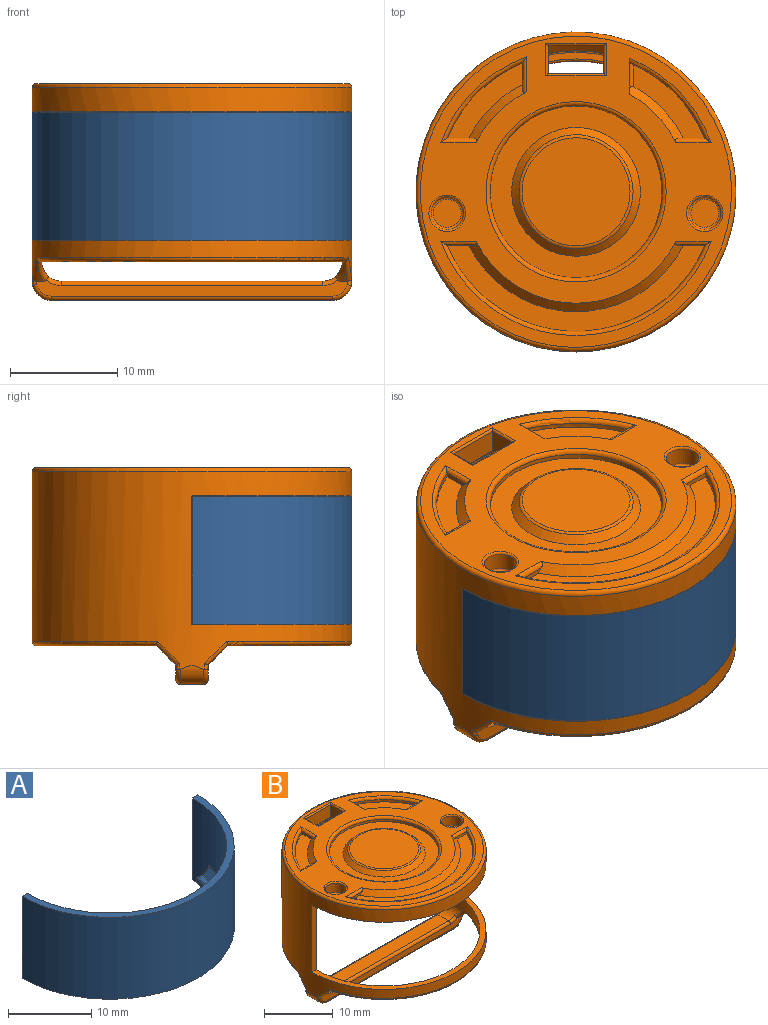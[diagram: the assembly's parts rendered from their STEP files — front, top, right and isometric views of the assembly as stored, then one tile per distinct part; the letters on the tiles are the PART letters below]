
ASSEMBLY  parts=2 mates=1
PART A: 37 faces, bbox 100.4x15.2x41.7 mm
  f0: cylinder r=14mm len=28mm, axis (0,0,-1), area 449mm2, adj f8,f9,f10,f11,f25,f26,f29,f30
  f1: plane 25.27x10.03mm, normal (0,0,1), area 20.8mm2, adj f12,f13,f14,f15
  f2: cylinder r=12.2mm len=23.68mm, axis (0,0,-1), area 16.2mm2, adj f13,f21,f22,f23
  f3: plane 26.8x10.82mm, normal (0,0,-1), area 48.7mm2, adj f22,f31,f32,f36
  f4: plane 1.36x1.12mm, normal (-0.22,0.97,0), area 0.9mm2, adj f14,f19,f23,f24,f32,f33
  f5: cone r=13.1mm half-angle=45deg, axis (0,0,1), area 39.9mm2, adj f15,f20,f24,f25
  f6: plane 1.36x1.12mm, normal (0.22,0.97,0), area 0.9mm2, adj f12,f16,f20,f21,f30,f31
  f7: cylinder r=14.9mm len=29.8mm, axis (0,0,-1), area 561.7mm2, adj f8,f9,f10,f11
  f8: plane 12x0.9mm, normal (0,1,0), area 10.8mm2, adj f0,f7,f10,f11
  f9: plane 12x0.9mm, normal (0,1,0), area 10.8mm2, adj f0,f7,f10,f11
  f10: plane 29.8x14.9mm, normal (0,0,-1), area 40.9mm2, adj f0,f7,f8,f9
  f11: plane 29.8x14.9mm, normal (0,0,1), area 40.9mm2, adj f0,f7,f8,f9
  f12: cylinder r=0.2mm len=0.65mm, axis (0.97,-0.22,0), area 0.2mm2, adj f1,f6,f16,f17
  f13: torus R=12.4mm, axis (0,0,-1), area 10.2mm2, adj f1,f2,f17,f18
  f14: cylinder r=0.2mm len=0.65mm, axis (0.97,0.22,0), area 0.2mm2, adj f1,f4,f18,f19
  f15: torus R=13.02mm, axis (0,0,-1), area 5.5mm2, adj f1,f5,f16,f19
  f16: bspline ~0.39x0.28mm, area 0.1mm2, adj f6,f12,f15,f20
  f17: sphere r=0.2mm, area 0.1mm2, adj f12,f13,f21
  f18: sphere r=0.2mm, area 0mm2, adj f13,f14,f23
  f19: bspline ~0.4x0.29mm, area 0.1mm2, adj f4,f14,f15,f24
  f20: bspline ~41.73x40.71mm, area 0.3mm2, adj f5,f6,f16,f26
  f21: cylinder r=0.2mm len=0.5mm, axis (0,0,-1), area 0.2mm2, adj f2,f6,f17,f27
  f22: torus R=12.4mm, axis (0,0,1), area 10.2mm2, adj f2,f3,f27,f28
  f23: cylinder r=0.2mm len=0.5mm, axis (0,0,-1), area 0.2mm2, adj f2,f4,f18,f28
  f24: bspline ~41.73x40.71mm, area 0.3mm2, adj f4,f5,f19,f29
  f25: torus R=13.8mm, axis (0,0,-1), area 5.8mm2, adj f0,f5,f26,f29
  f26: bspline ~0.74x0.44mm, area 0.1mm2, adj f0,f20,f25,f30
  f27: sphere r=0.2mm, area 0.1mm2, adj f21,f22,f31
  f28: sphere r=0.2mm, area 0mm2, adj f22,f23,f32
  f29: bspline ~0.64x0.46mm, area 0.1mm2, adj f0,f24,f25,f33
  f30: cylinder r=0.2mm len=1.12mm, axis (0,0,-1), area 0.4mm2, adj f0,f6,f26,f34
  f31: cylinder r=0.2mm len=1.41mm, axis (-0.97,0.22,0), area 0.4mm2, adj f3,f6,f27,f34
  f32: cylinder r=0.2mm len=1.41mm, axis (-0.97,-0.22,0), area 0.4mm2, adj f3,f4,f28,f35
  f33: cylinder r=0.2mm len=1.12mm, axis (0,0,-1), area 0.4mm2, adj f0,f4,f29,f35
  f34: bspline ~0.48x0.47mm, area 0.1mm2, adj f0,f30,f31,f36
  f35: bspline ~0.49x0.46mm, area 0.1mm2, adj f0,f32,f33,f36
  f36: torus R=13.8mm, axis (0,0,1), area 11.6mm2, adj f0,f3,f34,f35
PART B: 308 faces, bbox 100.4x32.3x47 mm
  f0: plane 29x29mm, normal (0,0,1), area 265.2mm2, adj f227,f264,f266,f274,f275,f276,f277,f285
  f1: plane 4.72x0.2mm, normal (0,0,-1), area 0.6mm2, adj f2,f268
  f2: cylinder r=14mm len=28mm, axis (0,0,-1), area 616.2mm2, adj f1,f179,f180,f182,f183,f184,f186,f198
  f3: plane 1.4x0.2mm, normal (-1,0,0), area 0.3mm2, adj f4,f6,f7,f173
  f4: plane 0.4x0.2mm, normal (0,1,0), area 0.1mm2, adj f3,f5,f7,f173
  f5: plane 1.4x0.2mm, normal (1,0,0), area 0.3mm2, adj f4,f6,f7,f173
  f6: plane 0.4x0.2mm, normal (0,-1,0), area 0.1mm2, adj f3,f5,f7,f173
  f7: plane 1.4x0.4mm, normal (0,0,-1), area 0.6mm2, adj f3,f4,f5,f6
  f8: plane 1.4x0.2mm, normal (-1,0,0), area 0.3mm2, adj f9,f11,f12,f173
  f9: plane 0.4x0.2mm, normal (0,1,0), area 0.1mm2, adj f8,f10,f12,f173
  f10: plane 1.4x0.2mm, normal (1,0,0), area 0.3mm2, adj f9,f11,f12,f173
  f11: plane 0.4x0.2mm, normal (0,-1,0), area 0.1mm2, adj f8,f10,f12,f173
  f12: plane 1.4x0.4mm, normal (0,0,-1), area 0.6mm2, adj f8,f9,f10,f11
  f13: plane 1.4x0.2mm, normal (-1,0,0), area 0.3mm2, adj f14,f16,f17,f173
  f14: plane 0.4x0.2mm, normal (0,1,0), area 0.1mm2, adj f13,f15,f17,f173
  f15: plane 1.4x0.2mm, normal (1,0,0), area 0.3mm2, adj f14,f16,f17,f173
  f16: plane 0.4x0.2mm, normal (0,-1,0), area 0.1mm2, adj f13,f15,f17,f173
  f17: plane 1.4x0.4mm, normal (0,0,-1), area 0.6mm2, adj f13,f14,f15,f16
  f18: plane 1.4x0.2mm, normal (-1,0,0), area 0.3mm2, adj f19,f21,f22,f173
  f19: plane 0.4x0.2mm, normal (0,1,0), area 0.1mm2, adj f18,f20,f22,f173
  f20: plane 1.4x0.2mm, normal (1,0,0), area 0.3mm2, adj f19,f21,f22,f173
  f21: plane 0.4x0.2mm, normal (0,-1,0), area 0.1mm2, adj f18,f20,f22,f173
  f22: plane 1.4x0.4mm, normal (0,0,-1), area 0.6mm2, adj f18,f19,f20,f21
  f23: plane 1.4x0.2mm, normal (-1,0,0), area 0.3mm2, adj f24,f26,f27,f173
  f24: plane 0.4x0.2mm, normal (0,1,0), area 0.1mm2, adj f23,f25,f27,f173
  f25: plane 1.4x0.2mm, normal (1,0,0), area 0.3mm2, adj f24,f26,f27,f173
  f26: plane 0.4x0.2mm, normal (0,-1,0), area 0.1mm2, adj f23,f25,f27,f173
  f27: plane 1.4x0.4mm, normal (0,0,-1), area 0.6mm2, adj f23,f24,f25,f26
  f28: plane 1.4x0.2mm, normal (-1,0,0), area 0.3mm2, adj f29,f31,f32,f173
  f29: plane 0.4x0.2mm, normal (0,1,0), area 0.1mm2, adj f28,f30,f32,f173
  f30: plane 1.4x0.2mm, normal (1,0,0), area 0.3mm2, adj f29,f31,f32,f173
  f31: plane 0.4x0.2mm, normal (0,-1,0), area 0.1mm2, adj f28,f30,f32,f173
  f32: plane 1.4x0.4mm, normal (0,0,-1), area 0.6mm2, adj f28,f29,f30,f31
  f33: plane 1.4x0.2mm, normal (-1,0,0), area 0.3mm2, adj f34,f36,f37,f173
  f34: plane 0.4x0.2mm, normal (0,1,0), area 0.1mm2, adj f33,f35,f37,f173
  f35: plane 1.4x0.2mm, normal (1,0,0), area 0.3mm2, adj f34,f36,f37,f173
  f36: plane 0.4x0.2mm, normal (0,-1,0), area 0.1mm2, adj f33,f35,f37,f173
  f37: plane 1.4x0.4mm, normal (0,0,-1), area 0.6mm2, adj f33,f34,f35,f36
  f38: plane 1.4x0.2mm, normal (-1,0,0), area 0.3mm2, adj f39,f41,f42,f173
  f39: plane 0.4x0.2mm, normal (0,1,0), area 0.1mm2, adj f38,f40,f42,f173
  f40: plane 1.4x0.2mm, normal (1,0,0), area 0.3mm2, adj f39,f41,f42,f173
  f41: plane 0.4x0.2mm, normal (0,-1,0), area 0.1mm2, adj f38,f40,f42,f173
  f42: plane 1.4x0.4mm, normal (0,0,-1), area 0.6mm2, adj f38,f39,f40,f41
  f43: plane 1.4x0.2mm, normal (-1,0,0), area 0.3mm2, adj f44,f46,f47,f173
  f44: plane 0.4x0.2mm, normal (0,1,0), area 0.1mm2, adj f43,f45,f47,f173
  f45: plane 1.4x0.2mm, normal (1,0,0), area 0.3mm2, adj f44,f46,f47,f173
  f46: plane 0.4x0.2mm, normal (0,-1,0), area 0.1mm2, adj f43,f45,f47,f173
  f47: plane 1.4x0.4mm, normal (0,0,-1), area 0.6mm2, adj f43,f44,f45,f46
  f48: plane 1.4x0.2mm, normal (-1,0,0), area 0.3mm2, adj f49,f51,f52,f173
  f49: plane 0.4x0.2mm, normal (0,1,0), area 0.1mm2, adj f48,f50,f52,f173
  f50: plane 1.4x0.2mm, normal (1,0,0), area 0.3mm2, adj f49,f51,f52,f173
  f51: plane 0.4x0.2mm, normal (0,-1,0), area 0.1mm2, adj f48,f50,f52,f173
  f52: plane 1.4x0.4mm, normal (0,0,-1), area 0.6mm2, adj f48,f49,f50,f51
  f53: plane 1.4x0.2mm, normal (-1,0,0), area 0.3mm2, adj f54,f56,f57,f173
  f54: plane 0.4x0.2mm, normal (0,1,0), area 0.1mm2, adj f53,f55,f57,f173
  f55: plane 1.4x0.2mm, normal (1,0,0), area 0.3mm2, adj f54,f56,f57,f173
  f56: plane 0.4x0.2mm, normal (0,-1,0), area 0.1mm2, adj f53,f55,f57,f173
  f57: plane 1.4x0.4mm, normal (0,0,-1), area 0.6mm2, adj f53,f54,f55,f56
  f58: plane 1.4x0.2mm, normal (-1,0,0), area 0.3mm2, adj f59,f61,f62,f173
  f59: plane 0.4x0.2mm, normal (0,1,0), area 0.1mm2, adj f58,f60,f62,f173
  f60: plane 1.4x0.2mm, normal (1,0,0), area 0.3mm2, adj f59,f61,f62,f173
  f61: plane 0.4x0.2mm, normal (0,-1,0), area 0.1mm2, adj f58,f60,f62,f173
  f62: plane 1.4x0.4mm, normal (0,0,-1), area 0.6mm2, adj f58,f59,f60,f61
  f63: plane 1.4x0.2mm, normal (-1,0,0), area 0.3mm2, adj f64,f66,f67,f173
  f64: plane 0.4x0.2mm, normal (0,1,0), area 0.1mm2, adj f63,f65,f67,f173
  f65: plane 1.4x0.2mm, normal (1,0,0), area 0.3mm2, adj f64,f66,f67,f173
  f66: plane 0.4x0.2mm, normal (0,-1,0), area 0.1mm2, adj f63,f65,f67,f173
  f67: plane 1.4x0.4mm, normal (0,0,-1), area 0.6mm2, adj f63,f64,f65,f66
  f68: plane 1.4x0.2mm, normal (-1,0,0), area 0.3mm2, adj f69,f71,f72,f173
  f69: plane 0.4x0.2mm, normal (0,1,0), area 0.1mm2, adj f68,f70,f72,f173
  f70: plane 1.4x0.2mm, normal (1,0,0), area 0.3mm2, adj f69,f71,f72,f173
  f71: plane 0.4x0.2mm, normal (0,-1,0), area 0.1mm2, adj f68,f70,f72,f173
  f72: plane 1.4x0.4mm, normal (0,0,-1), area 0.6mm2, adj f68,f69,f70,f71
  f73: plane 1.4x0.2mm, normal (-1,0,0), area 0.3mm2, adj f74,f76,f77,f173
  f74: plane 0.4x0.2mm, normal (0,1,0), area 0.1mm2, adj f73,f75,f77,f173
  f75: plane 1.4x0.2mm, normal (1,0,0), area 0.3mm2, adj f74,f76,f77,f173
  f76: plane 0.4x0.2mm, normal (0,-1,0), area 0.1mm2, adj f73,f75,f77,f173
  f77: plane 1.4x0.4mm, normal (0,0,-1), area 0.6mm2, adj f73,f74,f75,f76
  f78: plane 1.4x0.2mm, normal (-1,0,0), area 0.3mm2, adj f79,f81,f82,f173
  f79: plane 0.4x0.2mm, normal (0,1,0), area 0.1mm2, adj f78,f80,f82,f173
  f80: plane 1.4x0.2mm, normal (1,0,0), area 0.3mm2, adj f79,f81,f82,f173
  f81: plane 0.4x0.2mm, normal (0,-1,0), area 0.1mm2, adj f78,f80,f82,f173
  f82: plane 1.4x0.4mm, normal (0,0,-1), area 0.6mm2, adj f78,f79,f80,f81
  f83: plane 1.4x0.2mm, normal (-1,0,0), area 0.3mm2, adj f84,f86,f87,f173
  f84: plane 0.4x0.2mm, normal (0,1,0), area 0.1mm2, adj f83,f85,f87,f173
  f85: plane 1.4x0.2mm, normal (1,0,0), area 0.3mm2, adj f84,f86,f87,f173
  f86: plane 0.4x0.2mm, normal (0,-1,0), area 0.1mm2, adj f83,f85,f87,f173
  f87: plane 1.4x0.4mm, normal (0,0,-1), area 0.6mm2, adj f83,f84,f85,f86
  f88: plane 1.4x0.2mm, normal (-1,0,0), area 0.3mm2, adj f89,f91,f92,f173
  f89: plane 0.4x0.2mm, normal (0,1,0), area 0.1mm2, adj f88,f90,f92,f173
  f90: plane 1.4x0.2mm, normal (1,0,0), area 0.3mm2, adj f89,f91,f92,f173
  f91: plane 0.4x0.2mm, normal (0,-1,0), area 0.1mm2, adj f88,f90,f92,f173
  f92: plane 1.4x0.4mm, normal (0,0,-1), area 0.6mm2, adj f88,f89,f90,f91
  f93: plane 1.4x0.2mm, normal (-1,0,0), area 0.3mm2, adj f94,f96,f97,f173
  f94: plane 0.4x0.2mm, normal (0,1,0), area 0.1mm2, adj f93,f95,f97,f173
  f95: plane 1.4x0.2mm, normal (1,0,0), area 0.3mm2, adj f94,f96,f97,f173
  f96: plane 0.4x0.2mm, normal (0,-1,0), area 0.1mm2, adj f93,f95,f97,f173
  f97: plane 1.4x0.4mm, normal (0,0,-1), area 0.6mm2, adj f93,f94,f95,f96
  f98: plane 1.4x0.2mm, normal (-1,0,0), area 0.3mm2, adj f99,f101,f102,f173
  f99: plane 0.4x0.2mm, normal (0,1,0), area 0.1mm2, adj f98,f100,f102,f173
  f100: plane 1.4x0.2mm, normal (1,0,0), area 0.3mm2, adj f99,f101,f102,f173
  f101: plane 0.4x0.2mm, normal (0,-1,0), area 0.1mm2, adj f98,f100,f102,f173
  f102: plane 1.4x0.4mm, normal (0,0,-1), area 0.6mm2, adj f98,f99,f100,f101
  f103: plane 1.4x0.2mm, normal (-1,0,0), area 0.3mm2, adj f104,f106,f107,f173
  f104: plane 0.4x0.2mm, normal (0,1,0), area 0.1mm2, adj f103,f105,f107,f173
  f105: plane 1.4x0.2mm, normal (1,0,0), area 0.3mm2, adj f104,f106,f107,f173
  f106: plane 0.4x0.2mm, normal (0,-1,0), area 0.1mm2, adj f103,f105,f107,f173
  f107: plane 1.4x0.4mm, normal (0,0,-1), area 0.6mm2, adj f103,f104,f105,f106
  f108: plane 1.4x0.2mm, normal (-1,0,0), area 0.3mm2, adj f109,f111,f112,f173
  f109: plane 0.4x0.2mm, normal (0,1,0), area 0.1mm2, adj f108,f110,f112,f173
  f110: plane 1.4x0.2mm, normal (1,0,0), area 0.3mm2, adj f109,f111,f112,f173
  f111: plane 0.4x0.2mm, normal (0,-1,0), area 0.1mm2, adj f108,f110,f112,f173
  f112: plane 1.4x0.4mm, normal (0,0,-1), area 0.6mm2, adj f108,f109,f110,f111
  f113: plane 1.4x0.2mm, normal (-1,0,0), area 0.3mm2, adj f114,f116,f117,f173
  f114: plane 0.4x0.2mm, normal (0,1,0), area 0.1mm2, adj f113,f115,f117,f173
  f115: plane 1.4x0.2mm, normal (1,0,0), area 0.3mm2, adj f114,f116,f117,f173
  f116: plane 0.4x0.2mm, normal (0,-1,0), area 0.1mm2, adj f113,f115,f117,f173
  f117: plane 1.4x0.4mm, normal (0,0,-1), area 0.6mm2, adj f113,f114,f115,f116
  f118: plane 1.4x0.2mm, normal (-1,0,0), area 0.3mm2, adj f119,f121,f122,f173
  f119: plane 0.4x0.2mm, normal (0,1,0), area 0.1mm2, adj f118,f120,f122,f173
  f120: plane 1.4x0.2mm, normal (1,0,0), area 0.3mm2, adj f119,f121,f122,f173
  f121: plane 0.4x0.2mm, normal (0,-1,0), area 0.1mm2, adj f118,f120,f122,f173
  f122: plane 1.4x0.4mm, normal (0,0,-1), area 0.6mm2, adj f118,f119,f120,f121
  f123: plane 1.4x0.2mm, normal (-1,0,0), area 0.3mm2, adj f124,f126,f127,f173
  f124: plane 0.4x0.2mm, normal (0,1,0), area 0.1mm2, adj f123,f125,f127,f173
  f125: plane 1.4x0.2mm, normal (1,0,0), area 0.3mm2, adj f124,f126,f127,f173
  f126: plane 0.4x0.2mm, normal (0,-1,0), area 0.1mm2, adj f123,f125,f127,f173
  f127: plane 1.4x0.4mm, normal (0,0,-1), area 0.6mm2, adj f123,f124,f125,f126
  f128: plane 1.4x0.2mm, normal (-1,0,0), area 0.3mm2, adj f129,f131,f132,f173
  f129: plane 0.4x0.2mm, normal (0,1,0), area 0.1mm2, adj f128,f130,f132,f173
  f130: plane 1.4x0.2mm, normal (1,0,0), area 0.3mm2, adj f129,f131,f132,f173
  f131: plane 0.4x0.2mm, normal (0,-1,0), area 0.1mm2, adj f128,f130,f132,f173
  f132: plane 1.4x0.4mm, normal (0,0,-1), area 0.6mm2, adj f128,f129,f130,f131
  f133: plane 1.4x0.2mm, normal (-1,0,0), area 0.3mm2, adj f134,f136,f137,f173
  f134: plane 0.4x0.2mm, normal (0,1,0), area 0.1mm2, adj f133,f135,f137,f173
  f135: plane 1.4x0.2mm, normal (1,0,0), area 0.3mm2, adj f134,f136,f137,f173
  f136: plane 0.4x0.2mm, normal (0,-1,0), area 0.1mm2, adj f133,f135,f137,f173
  f137: plane 1.4x0.4mm, normal (0,0,-1), area 0.6mm2, adj f133,f134,f135,f136
  f138: plane 1.4x0.2mm, normal (-1,0,0), area 0.3mm2, adj f139,f141,f142,f173
  f139: plane 0.4x0.2mm, normal (0,1,0), area 0.1mm2, adj f138,f140,f142,f173
  f140: plane 1.4x0.2mm, normal (1,0,0), area 0.3mm2, adj f139,f141,f142,f173
  f141: plane 0.4x0.2mm, normal (0,-1,0), area 0.1mm2, adj f138,f140,f142,f173
  f142: plane 1.4x0.4mm, normal (0,0,-1), area 0.6mm2, adj f138,f139,f140,f141
  f143: plane 1.4x0.2mm, normal (-1,0,0), area 0.3mm2, adj f144,f146,f147,f173
  f144: plane 0.4x0.2mm, normal (0,1,0), area 0.1mm2, adj f143,f145,f147,f173
  f145: plane 1.4x0.2mm, normal (1,0,0), area 0.3mm2, adj f144,f146,f147,f173
  f146: plane 0.4x0.2mm, normal (0,-1,0), area 0.1mm2, adj f143,f145,f147,f173
  f147: plane 1.4x0.4mm, normal (0,0,-1), area 0.6mm2, adj f143,f144,f145,f146
  f148: plane 1.4x0.2mm, normal (-1,0,0), area 0.3mm2, adj f149,f151,f152,f173
  f149: plane 0.4x0.2mm, normal (0,1,0), area 0.1mm2, adj f148,f150,f152,f173
  f150: plane 1.4x0.2mm, normal (1,0,0), area 0.3mm2, adj f149,f151,f152,f173
  f151: plane 0.4x0.2mm, normal (0,-1,0), area 0.1mm2, adj f148,f150,f152,f173
  f152: plane 1.4x0.4mm, normal (0,0,-1), area 0.6mm2, adj f148,f149,f150,f151
  f153: plane 1.4x0.2mm, normal (-1,0,0), area 0.3mm2, adj f154,f156,f157,f173
  f154: plane 0.4x0.2mm, normal (0,1,0), area 0.1mm2, adj f153,f155,f157,f173
  f155: plane 1.4x0.2mm, normal (1,0,0), area 0.3mm2, adj f154,f156,f157,f173
  f156: plane 0.4x0.2mm, normal (0,-1,0), area 0.1mm2, adj f153,f155,f157,f173
  f157: plane 1.4x0.4mm, normal (0,0,-1), area 0.6mm2, adj f153,f154,f155,f156
  f158: plane 1.4x0.2mm, normal (-1,0,0), area 0.3mm2, adj f159,f161,f162,f173
  f159: plane 0.4x0.2mm, normal (0,1,0), area 0.1mm2, adj f158,f160,f162,f173
  f160: plane 1.4x0.2mm, normal (1,0,0), area 0.3mm2, adj f159,f161,f162,f173
  f161: plane 0.4x0.2mm, normal (0,-1,0), area 0.1mm2, adj f158,f160,f162,f173
  f162: plane 1.4x0.4mm, normal (0,0,-1), area 0.6mm2, adj f158,f159,f160,f161
  f163: plane 1.4x0.2mm, normal (-1,0,0), area 0.3mm2, adj f164,f166,f167,f173
  f164: plane 0.4x0.2mm, normal (0,1,0), area 0.1mm2, adj f163,f165,f167,f173
  f165: plane 1.4x0.2mm, normal (1,0,0), area 0.3mm2, adj f164,f166,f167,f173
  f166: plane 0.4x0.2mm, normal (0,-1,0), area 0.1mm2, adj f163,f165,f167,f173
  f167: plane 1.4x0.4mm, normal (0,0,-1), area 0.6mm2, adj f163,f164,f165,f166
  f168: plane 1.4x0.2mm, normal (-1,0,0), area 0.3mm2, adj f169,f171,f172,f173
  f169: plane 0.4x0.2mm, normal (0,1,0), area 0.1mm2, adj f168,f170,f172,f173
  f170: plane 1.4x0.2mm, normal (1,0,0), area 0.3mm2, adj f169,f171,f172,f173
  f171: plane 0.4x0.2mm, normal (0,-1,0), area 0.1mm2, adj f168,f170,f172,f173
  f172: plane 1.4x0.4mm, normal (0,0,-1), area 0.6mm2, adj f168,f169,f170,f171
  f173: plane 26.2x2.2mm, normal (0,0,-1), area 38mm2, adj f3,f4,f5,f6,f8,f9,f10,f11
  f174: cylinder r=1.8mm len=2.2mm, axis (0,1,0), area 5.8mm2, adj f173,f181,f218,f222
  f175: cylinder r=1.8mm len=2.2mm, axis (0,1,0), area 5.8mm2, adj f173,f181,f215,f226
  f176: plane 28.92x1.49mm, normal (0,-1,0), area 29.3mm2, adj f207,f210,f219,f220,f222,f223,f224,f225
  f177: plane 28.92x1.49mm, normal (0,1,0), area 29.3mm2, adj f208,f209,f211,f213,f214,f215,f216,f217
  f178: plane 28.32x12.16mm, normal (0,0,-1), area 11.8mm2, adj f184,f186,f212,f228,f234,f238
  f179: plane 28.32x14.53mm, normal (0,0,-1), area 20mm2, adj f2,f184,f186,f221,f229,f233
  f180: plane 29.8x14.9mm, normal (0,0,1), area 40.9mm2, adj f2,f181,f182,f183
  f181: cylinder r=14.9mm len=29.8mm, axis (0,0,-1), area 936.9mm2, adj f174,f175,f180,f182,f183,f198,f211,f212
  f182: plane 12x0.9mm, normal (0,-1,0), area 10.8mm2, adj f2,f180,f181,f198
  f183: plane 12x0.9mm, normal (0,-1,0), area 10.8mm2, adj f2,f180,f181,f198
  f184: cylinder r=1.8mm len=5.47mm, axis (0,1,0), area 8.9mm2, adj f2,f178,f179,f185,f228,f232,f233,f237
  f185: plane 24.4x2.2mm, normal (0,0,1), area 53.7mm2, adj f184,f186,f231,f236
  f186: cylinder r=1.8mm len=5.47mm, axis (0,1,0), area 8.9mm2, adj f2,f178,f179,f185,f228,f229,f230,f234
  f187: plane 1.4x0.2mm, normal (-1,0,0), area 0.3mm2, adj f173,f188,f190,f191
  f188: plane 0.4x0.2mm, normal (0,1,0), area 0.1mm2, adj f173,f187,f189,f191
  f189: plane 1.4x0.2mm, normal (1,0,0), area 0.3mm2, adj f173,f188,f190,f191
  f190: plane 0.4x0.2mm, normal (0,-1,0), area 0.1mm2, adj f173,f187,f189,f191
  f191: plane 1.4x0.4mm, normal (0,0,-1), area 0.6mm2, adj f187,f188,f189,f190
  f192: plane 26.8x10.82mm, normal (0,0,-1), area 48.7mm2, adj f250,f251,f259,f260
  f193: cone r=13.1mm half-angle=45deg, axis (0,0,1), area 39.9mm2, adj f247,f248,f257,f258
  f194: plane 25.27x10.03mm, normal (0,0,1), area 20.8mm2, adj f240,f242,f246,f247
  f195: cylinder r=12.2mm len=23.68mm, axis (0,0,-1), area 16.2mm2, adj f241,f242,f251,f252
  f196: plane 1.36x1.12mm, normal (-0.22,-0.97,0), area 0.9mm2, adj f240,f241,f243,f248,f249,f250
  f197: plane 1.36x1.12mm, normal (0.22,-0.97,0), area 0.9mm2, adj f246,f252,f253,f257,f260,f263
  f198: plane 29.8x28.62mm, normal (0,0,-1), area 639.2mm2, adj f2,f181,f182,f183,f271,f272,f273
  f199: plane 2.6x2.2mm, normal (1,0,0), area 5.7mm2, adj f200,f201,f272,f275
  f200: plane 5.2x2.2mm, normal (0,-1,0), area 11.4mm2, adj f199,f202,f268,f269,f270,f271,f272,f274
  f201: plane 5.2x2.2mm, normal (0,1,0), area 11.4mm2, adj f199,f202,f273,f277
  f202: plane 2.6x2.2mm, normal (-1,0,0), area 5.7mm2, adj f200,f201,f271,f276
  f203: cylinder r=1.5mm len=3mm, axis (0,0,1), area 15.1mm2, adj f264,f265
  f204: plane 2.6x2.6mm, normal (0,0,1), area 5.3mm2, adj f265
  f205: cylinder r=1.5mm len=3mm, axis (0,0,1), area 15.1mm2, adj f266,f267
  f206: plane 2.6x2.6mm, normal (0,0,1), area 5.3mm2, adj f267
  f207: plane 0.98x0.98mm, normal (0,-0.71,-0.71), area 0.4mm2, adj f176,f223,f233
  f208: plane 0.98x0.98mm, normal (0,0.71,-0.71), area 0.4mm2, adj f177,f211,f238
  f209: plane 0.98x0.98mm, normal (0,0.71,-0.71), area 0.4mm2, adj f177,f214,f234
  f210: plane 0.98x0.98mm, normal (0,-0.71,-0.71), area 0.4mm2, adj f176,f219,f229
  f211: bspline ~2.32x2.29mm, area 1.5mm2, adj f177,f181,f208,f212,f213,f238
  f212: torus R=14.5mm, axis (0,0,1), area 25mm2, adj f178,f181,f211,f214,f234,f238
  f213: cylinder r=0.4mm len=0.55mm, axis (0,0,-1), area 0.3mm2, adj f177,f181,f211,f215
  f214: bspline ~2.32x2.29mm, area 1.5mm2, adj f177,f181,f209,f212,f216,f234
  f215: torus R=1.4mm, axis (0,-1,0), area 1.4mm2, adj f175,f177,f181,f213,f217
  f216: cylinder r=0.4mm len=0.55mm, axis (0,0,-1), area 0.3mm2, adj f177,f181,f214,f218
  f217: cylinder r=0.4mm len=26.2mm, axis (1,0,0), area 16.5mm2, adj f173,f177,f215,f218
  f218: torus R=1.4mm, axis (0,-1,0), area 1.4mm2, adj f174,f177,f181,f216,f217
  f219: bspline ~2.32x2.29mm, area 1.5mm2, adj f176,f181,f210,f220,f221,f229
  f220: cylinder r=0.4mm len=0.55mm, axis (0,0,-1), area 0.3mm2, adj f176,f181,f219,f222
  f221: torus R=14.5mm, axis (0,0,1), area 25mm2, adj f179,f181,f219,f223,f229,f233
  f222: torus R=1.4mm, axis (0,-1,0), area 1.4mm2, adj f174,f176,f181,f220,f224
  f223: bspline ~2.32x2.29mm, area 1.5mm2, adj f176,f181,f207,f221,f225,f233
  f224: cylinder r=0.4mm len=26.2mm, axis (-1,0,0), area 16.5mm2, adj f173,f176,f222,f226
  f225: cylinder r=0.4mm len=0.55mm, axis (0,0,-1), area 0.3mm2, adj f176,f181,f223,f226
  f226: torus R=1.4mm, axis (0,-1,0), area 1.4mm2, adj f175,f176,f181,f224,f225
  f227: torus R=14.5mm, axis (0,0,1), area 58.2mm2, adj f0,f181
  f228: torus R=14.2mm, axis (0,0,1), area 13.1mm2, adj f2,f178,f184,f186
  f229: bspline ~2.23x2.17mm, area 1.7mm2, adj f176,f179,f186,f210,f219,f221,f230
  f230: torus R=2.2mm, axis (0,-1,0), area 0.8mm2, adj f176,f186,f229,f231
  f231: cylinder r=0.4mm len=24.4mm, axis (1,0,0), area 15.3mm2, adj f176,f185,f230,f232
  f232: torus R=2.2mm, axis (0,-1,0), area 0.8mm2, adj f176,f184,f231,f233
  f233: bspline ~2.23x2.17mm, area 1.7mm2, adj f176,f179,f184,f207,f221,f223,f232
  f234: bspline ~2.23x2.17mm, area 1.7mm2, adj f177,f178,f186,f209,f212,f214,f235
  f235: torus R=2.2mm, axis (0,-1,0), area 0.8mm2, adj f177,f186,f234,f236
  f236: cylinder r=0.4mm len=24.4mm, axis (-1,0,0), area 15.3mm2, adj f177,f185,f235,f237
  f237: torus R=2.2mm, axis (0,-1,0), area 0.8mm2, adj f177,f184,f236,f238
  f238: bspline ~2.23x2.17mm, area 1.7mm2, adj f177,f178,f184,f208,f211,f212,f237
  f239: sphere r=0.2mm, area 0.1mm2, adj f240,f241,f242
  f240: cylinder r=0.2mm len=0.65mm, axis (-0.97,0.22,0), area 0.2mm2, adj f194,f196,f239,f243
  f241: cylinder r=0.2mm len=0.5mm, axis (0,0,-1), area 0.2mm2, adj f195,f196,f239,f244
  f242: torus R=12.4mm, axis (0,0,-1), area 10.2mm2, adj f194,f195,f239,f245
  f243: bspline ~0.39x0.28mm, area 0.1mm2, adj f196,f240,f247,f248
  f244: sphere r=0.2mm, area 0.1mm2, adj f241,f250,f251
  f245: sphere r=0.2mm, area 0.1mm2, adj f242,f246,f252
  f246: cylinder r=0.2mm len=0.65mm, axis (-0.97,-0.22,0), area 0.2mm2, adj f194,f197,f245,f253
  f247: torus R=13.02mm, axis (0,0,-1), area 5.5mm2, adj f193,f194,f243,f253
  f248: bspline ~41.73x40.71mm, area 0.3mm2, adj f193,f196,f243,f254
  f249: cylinder r=0.2mm len=1.12mm, axis (0,0,-1), area 0.4mm2, adj f2,f196,f254,f255
  f250: cylinder r=0.2mm len=1.41mm, axis (0.97,-0.22,0), area 0.4mm2, adj f192,f196,f244,f255
  f251: torus R=12.4mm, axis (0,0,1), area 10.2mm2, adj f192,f195,f244,f256
  f252: cylinder r=0.2mm len=0.5mm, axis (0,0,-1), area 0.2mm2, adj f195,f197,f245,f256
  f253: bspline ~0.4x0.29mm, area 0.1mm2, adj f197,f246,f247,f257
  f254: bspline ~0.74x0.44mm, area 0.1mm2, adj f2,f248,f249,f258
  f255: bspline ~0.48x0.47mm, area 0.1mm2, adj f2,f249,f250,f259
  f256: sphere r=0.2mm, area 0.1mm2, adj f251,f252,f260
  f257: bspline ~41.73x40.71mm, area 0.3mm2, adj f193,f197,f253,f261
  f258: torus R=13.8mm, axis (0,0,-1), area 5.8mm2, adj f2,f193,f254,f261
  f259: torus R=13.8mm, axis (0,0,1), area 11.6mm2, adj f2,f192,f255,f262
  f260: cylinder r=0.2mm len=1.41mm, axis (0.97,0.22,0), area 0.4mm2, adj f192,f197,f256,f262
  f261: bspline ~0.64x0.46mm, area 0.1mm2, adj f2,f257,f258,f263
  f262: bspline ~0.49x0.46mm, area 0.1mm2, adj f2,f259,f260,f263
  f263: cylinder r=0.2mm len=1.12mm, axis (0,0,-1), area 0.4mm2, adj f2,f197,f261,f262
  f264: torus R=1.7mm, axis (0,0,1), area 3.1mm2, adj f0,f203
  f265: torus R=1.3mm, axis (0,0,1), area 2.8mm2, adj f203,f204
  f266: torus R=1.7mm, axis (0,0,1), area 3.1mm2, adj f0,f205
  f267: torus R=1.3mm, axis (0,0,1), area 2.8mm2, adj f205,f206
  f268: cylinder r=0.2mm len=4.72mm, axis (1,0,0), area 1.5mm2, adj f1,f200,f269,f270
  f269: bspline ~0.63x0.2mm, area 0.1mm2, adj f2,f200,f268,f271
  f270: bspline ~0.69x0.21mm, area 0.1mm2, adj f2,f200,f268,f272
  f271: cylinder r=0.2mm len=2.92mm, axis (0,-1,0), area 0.9mm2, adj f198,f200,f202,f269,f273
  f272: cylinder r=0.2mm len=2.92mm, axis (0,1,0), area 0.9mm2, adj f198,f199,f200,f270,f273
  f273: cylinder r=0.2mm len=5.6mm, axis (-1,0,0), area 1.7mm2, adj f198,f201,f271,f272
  f274: cylinder r=0.2mm len=5.6mm, axis (1,0,0), area 1.7mm2, adj f0,f200,f275,f276
  f275: cylinder r=0.2mm len=3mm, axis (0,1,0), area 0.9mm2, adj f0,f199,f274,f277
  f276: cylinder r=0.2mm len=3mm, axis (0,-1,0), area 0.9mm2, adj f0,f202,f274,f277
  f277: cylinder r=0.2mm len=5.6mm, axis (-1,0,0), area 1.7mm2, adj f0,f201,f275,f276
  f278: cylinder r=8mm len=16mm, axis (0,0,1), area 20.1mm2, adj f279,f307
  f279: plane 16x16mm, normal (0,0,1), area 88mm2, adj f278,f296
  f280: plane 10.07x10.07mm, normal (0,0,1), area 79.6mm2, adj f297
  f281: cylinder r=13mm len=7mm, axis (0,0,1), area 4.1mm2, adj f282,f283,f284,f305
  f282: plane 2.45x0.4mm, normal (0,1,0), area 0.9mm2, adj f281,f284,f295,f306
  f283: plane 2.45x0.4mm, normal (-1,0,0), area 0.9mm2, adj f281,f284,f295,f304
  f284: plane 7x7mm, normal (0,0,1), area 15.8mm2, adj f281,f282,f283,f295
  f285: plane 3.4x0.46mm, normal (1,0,0), area 1.1mm2, adj f0,f294,f301,f303
  f286: plane 2.45x0.4mm, normal (0,1,0), area 0.9mm2, adj f287,f288,f294,f302
  f287: cylinder r=13mm len=7mm, axis (0,0,1), area 4mm2, adj f286,f288,f301,f303
  f288: plane 6.83x6.6mm, normal (0,0,1), area 15mm2, adj f286,f287,f294,f303
  f289: plane 2.45x0.4mm, normal (0,-1,0), area 0.9mm2, adj f290,f292,f293,f300
  f290: cylinder r=13mm len=24mm, axis (0,0,1), area 12.2mm2, adj f289,f291,f292,f299
  f291: plane 2.45x0.4mm, normal (0,-1,0), area 0.9mm2, adj f290,f292,f293,f298
  f292: plane 24x8mm, normal (0,0,1), area 50.4mm2, adj f289,f290,f291,f293
  f293: cone r=10.38mm half-angle=45deg, axis (0,0,-1), area 26.7mm2, adj f0,f289,f291,f292,f298,f300
  f294: cone r=11.18mm half-angle=45deg, axis (0,0,-1), area 7.4mm2, adj f0,f285,f286,f288,f302,f303
  f295: cone r=11.18mm half-angle=45deg, axis (0,0,-1), area 7.5mm2, adj f0,f282,f283,f284,f304,f306
  f296: cone r=5.2mm half-angle=45deg, axis (0,0,-1), area 34.3mm2, adj f279,f297
  f297: torus R=5.03mm, axis (0,0,1), area 10.2mm2, adj f280,f296
  f298: cylinder r=0.4mm len=3.28mm, axis (1,0,0), area 1.8mm2, adj f0,f291,f293,f299
  f299: torus R=13.4mm, axis (0,0,1), area 19.8mm2, adj f0,f290,f298,f300
  f300: cylinder r=0.4mm len=3.28mm, axis (1,0,0), area 1.8mm2, adj f0,f289,f293,f299
  f301: torus R=13.4mm, axis (0,0,1), area 6.7mm2, adj f0,f285,f287,f302
  f302: cylinder r=0.4mm len=3.28mm, axis (-1,0,0), area 1.8mm2, adj f0,f286,f294,f301
  f303: cylinder r=0.4mm len=2.45mm, axis (0,-1,0), area 1.4mm2, adj f285,f287,f288,f294
  f304: cylinder r=0.4mm len=3.28mm, axis (0,-1,0), area 1.8mm2, adj f0,f283,f295,f305
  f305: torus R=13.4mm, axis (0,0,1), area 6.8mm2, adj f0,f281,f304,f306
  f306: cylinder r=0.4mm len=3.28mm, axis (-1,0,0), area 1.8mm2, adj f0,f282,f295,f305
  f307: torus R=8.4mm, axis (0,0,1), area 32.2mm2, adj f0,f278
PLACE A t=(0,0,-0.05)mm
PLACE B at identity fixed
MATE slider A.f7 <-> B.f181  axis (0,0,-1) through (0,0,7.95)mm
